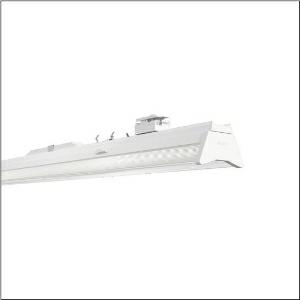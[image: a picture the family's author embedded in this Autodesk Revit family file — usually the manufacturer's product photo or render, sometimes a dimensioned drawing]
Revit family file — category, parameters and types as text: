
# Revit family: licross_r__21_performance_mo_52tm167n485g_c234
name_source: partatom
category: Lighting Fixtures
units: mm (PartAtom-declared; Revit-internal decimal feet)

## family parameters
Cut with Voids When Loaded = No
Host = Face
Light Source = No
Part Type = Normal
Room Calculation Point = No
Round Connector Dimension = Use Diameter
Shared = No

## types (1)
- Licross® 21 Performance MO (1 x LED, 8720 lm, 47.9 W, 4000K)
    Apparent Load = 48 VA
    CIE Flux Codes = 66 88 96 79 100
    Color Rendering = 80
    Color Temperature = 4000K
    Default Elevation = 1800 mm
    Description = Licross® 21 Performance MO, luminaire insert, of sheet steel, galvanised, coil coated, white, length: 1.500mm, width: 120mm, height: 123mm, LED rated luminous flux: 8.720lm, light colour: 840, control gear: ON/OFF, with plug, 3-pole, with phase selection, mains connection: 220..240V, AC, 50/60Hz, rated input power: 48W, internal wiring halogen-free, primary light control with lens, of plastic, primary optical cover: cover, of PMMA, light emission: direct/indirect distribution, primary light characteristic: symmetric, protection rating (complete): IP40, insulation class (complete): insulation class I (protective earthing), certification: CE, ENEC, UKCA, protection symbol: D if used in an environment without relevant dust loads with corresponding accessories, impact resistance: IK06, permissible ambient temperature for indoor applications: -35..+45°C, corresponds to IFS (International Featured Standards) requirements for safety and quality in the food industry, reducing of maximum allowable ambient temperature of 5°C with ceiling mounting, LABS conformity tested according to VDMA 24364:2018-05, packaging unit: 1 piece
    Height = 114 mm
    Lamp = 1 x LED
    Lamp Light Flux = 8720 lm
    Lamp Power = 47.9 W
    Lamp count = 1
    Length = 1500 mm
    Luminous efficacy = 182 lm/W
    Manufacturer = Siteco
    ModVariant = No
    Model = 52TM167N485G
    Mounting Place = Ceiling
    Mounting Type = Pendant
    Number of Poles = 1
    OnlyDefault = Yes
    Power Factor = 1
    Product Name = Licross® 21 Performance MO
    Product group = luminaire insert | ceiling pendant
    ProductGroupID = 902
    Protection Class = Protection class I
    Protection Degree = IP 40
    RLX_Detail_Level = 1
    RLX_Emergency_Light_Flux = 0 lm
    RLX_Emergency_Type = 0
    RLX_Emergency_Type_DB = No
    RlxData = <blob elided: 30341 chars, md5=17fb8b73>
    Socket = socket
    Standby Power = 0 W
    System Light Flux = 8720 lm
    System Power = 48 W
    Type Comments = Product without accessories
    Type Image = l_1256138.jpg
    URL = http://relux.com
    VarID = ---
    Voltage = 0 V
    Weight = 0.00 kg
    Width = 120 mm

## geometry (parser evidence)
native form markers: Blend x4, Sweep x10
no freeform markers — native parametric forms only
